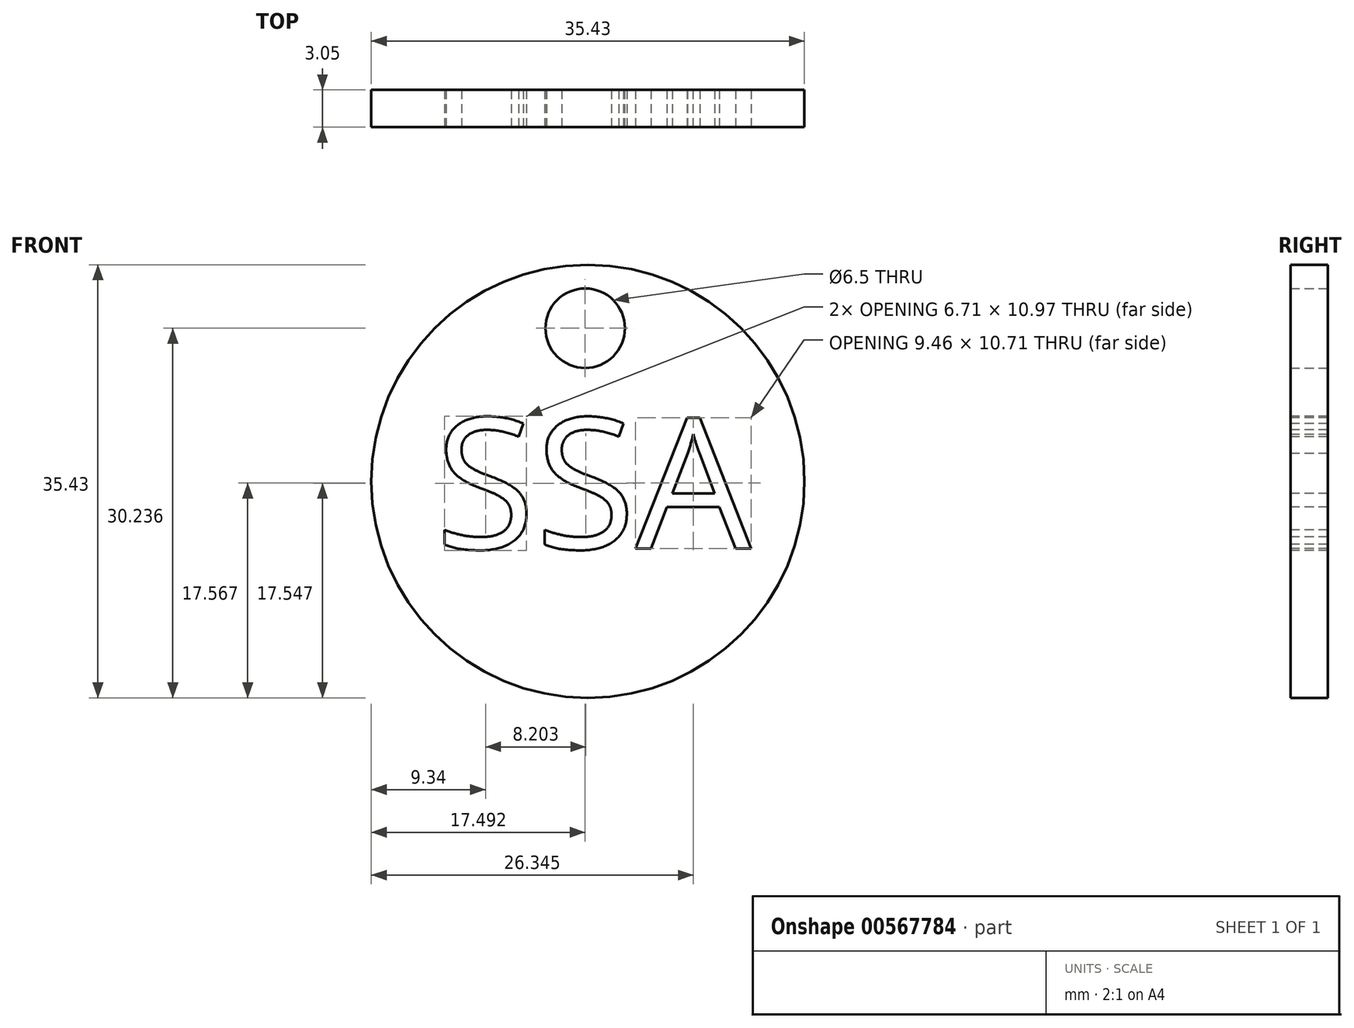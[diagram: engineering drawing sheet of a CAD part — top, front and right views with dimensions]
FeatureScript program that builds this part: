
annotation { "Feature Type Name" : "Feature", "Feature Type Description" : "" }
export const myFeature = defineFeature(function(context is Context, id is Id, definition is map)
    precondition{}
    {
        {
            var Q0;
            Q0=qCreatedBy(makeId("Front.planeOp"),FACE);
            var sketch = newSketch(context, id + "F0", { "sketchPlane" : qUnion([Q0])});
            skCircle(sketch, "E0", {"center": v(-12.27, -15.14) * mm, "radius": 17.72 * mm});
            skSolve(sketch);
        }
        {
            var Q0;
            Q0 = qSketchRegion(id + "F0", true);
            extrude(context, id + "F1", {"entities" : qUnion([Q0]), "depth" : 3.05 * mm, "offsetDistance" : 25.4 * mm});
        }
        {
            var Q0;
            Q0=makeQuery(id+"F1.opExtrude","CAP_FACE",FACE,{"disambiguationData":[OSD([sQuery(id+"F0.wireOp",EDGE,"E0")])],"isStart":false});
            var sketch = newSketch(context, id + "F2", { "sketchPlane" : qUnion([Q0])});
            skText(sketch, "E1", { "text": "SSA", "fontName": "OpenSans-Regular.ttf"});
            const initialGuessF2  = {"E1": [-0.02477, -0.02064, 1, 0, 0.01076]};
            skSetInitialGuess(sketch, initialGuessF2);
            skSolve(sketch);
        }
        {
            var Q0;
            Q0 = qSketchRegion(id + "F2", true);
            extrude(context, id + "F3", {"entities" : qUnion([Q0]), "operationType" : NewBodyOperationType.REMOVE, "oppositeDirection" : true, "depth" : 25.4 * mm, "offsetDistance" : 25.4 * mm});
        }
        {
            var Q0;
            Q0 = qSketchRegion(id + "F2", true);
            extrude(context, id + "F4", {"entities" : qUnion([Q0]), "operationType" : NewBodyOperationType.REMOVE, "oppositeDirection" : true, "depth" : 1.02 * mm, "offsetDistance" : 25.4 * mm});
        }
        {
            var Q0;
            Q0=qCreatedBy(makeId("Front.planeOp"),FACE);
            var sketch = newSketch(context, id + "F5", { "sketchPlane" : qUnion([Q0])});
            skCircle(sketch, "E2", {"center": v(-12.49, -2.61) * mm, "radius": 3.25 * mm});
            skSolve(sketch);
        }
        {
            var Q0;
            Q0 = qSketchRegion(id + "F5", true);
            extrude(context, id + "F6", {"entities" : qUnion([Q0]), "operationType" : NewBodyOperationType.REMOVE, "depth" : 3.8 * mm, "offsetDistance" : 25.4 * mm});
        }
    });
